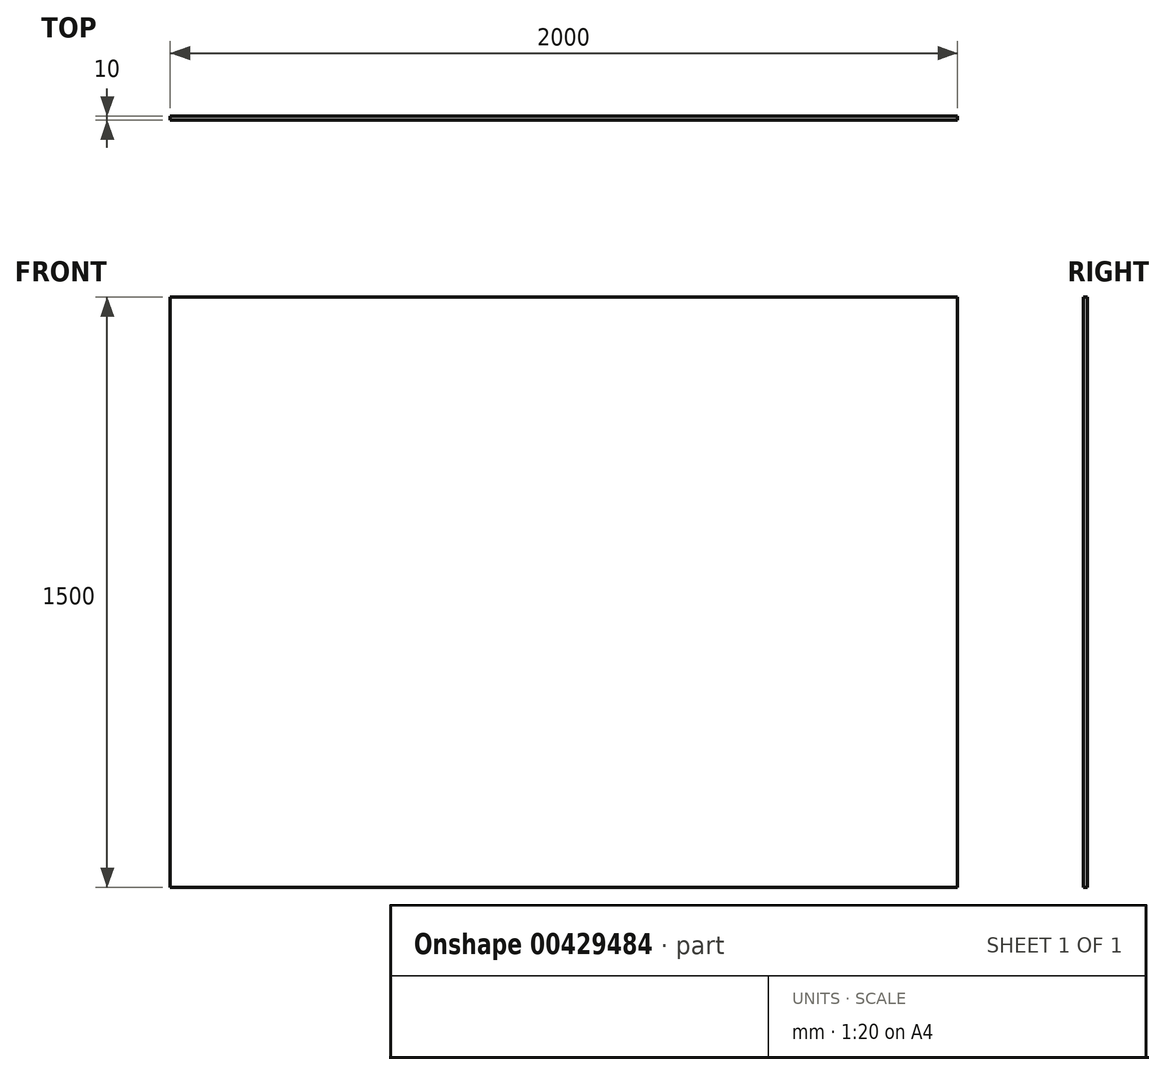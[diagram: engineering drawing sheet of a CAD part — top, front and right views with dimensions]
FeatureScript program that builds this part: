
annotation { "Feature Type Name" : "Feature", "Feature Type Description" : "" }
export const myFeature = defineFeature(function(context is Context, id is Id, definition is map)
    precondition{}
    {
        {
            var Q0;
            Q0=qCreatedBy(makeId("Front.planeOp"),FACE);
            var sketch = newSketch(context, id + "F0", { "sketchPlane" : qUnion([Q0])});
            skLineSegment(sketch, "E0.bottom", {"start": v(1000, 750) * mm, "end": v(-1000, 750) * mm});
            skLineSegment(sketch, "E0.top", {"start": v(1000, -750) * mm, "end": v(-1000, -750) * mm});
            skLineSegment(sketch, "E0.left", {"start": v(1000, 750) * mm, "end": v(1000, -750) * mm});
            skLineSegment(sketch, "E0.right", {"start": v(-1000, 750) * mm, "end": v(-1000, -750) * mm});
            skPoint(sketch, "E0.middle", {"position": v(0, 0) * mm});
            skSolve(sketch);
        }
        {
            var Q0;
            Q0 = qSketchRegion(id + "F0", true);
            extrude(context, id + "F1", {"entities" : qUnion([Q0]), "depth" : 10 * mm});
        }
    });
